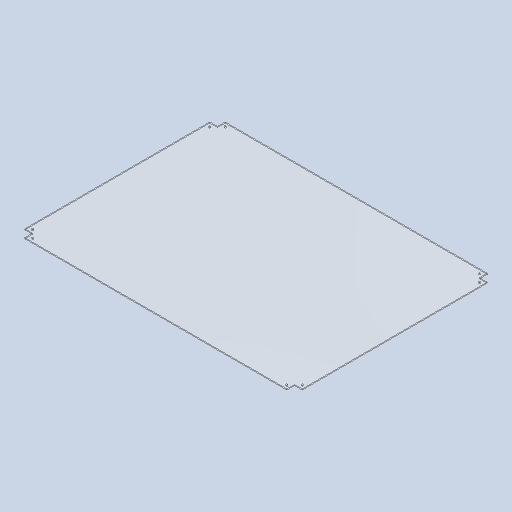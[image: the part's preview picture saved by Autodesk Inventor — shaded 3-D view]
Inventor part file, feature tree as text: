
AUTODESK INVENTOR PART (.ipt)
format: ipt  version: 2023 (Build 270158000, 158)  size: 128,512 bytes
history: native  units: in
note: dims shown in document units (in); Inventor stores cm internally (conversion verified against a paired STEP export)
features: extrude x1, sketch x1
ambient origin geometry x8: Origin, YZ Plane, XZ Plane, XY Plane, X Axis, Y Axis, Z Axis, Center Point
bodies: Solid1 (feature_tree)
feature tree (2):
  extrude  "Extrusion1"  Depth=26.0in
  sketch  "Sketch1"  dims[d0=36.0in d1=26.0in d2=1.0in d3=1.0in d4=1.0in d5=1.0in d6=1.0in d7=1.0in d8=1.0in d9=1.0in d10=0.1969in d11=0.5in d12=0.5in d13=0.1969in d14=0.5in d15=0.5in d16=0.1969in d17=0.1969in d18=0.5in d19=0.5in d20=0.5in d21=0.5in d22=0.125in d23=0.0in]
